# Revit family: Plumbing-Faucet-Sloan-Valve-EFX-380
name_source: partatom
category: Plumbing Fixtures
units: mm (PartAtom-declared; Revit-internal decimal feet)

## family parameters
Cut with Voids When Loaded = No
Host = Face
OmniClass Number = 23.45.55.14
OmniClass Title = Single Faucets
Part Type = Normal
Room Calculation Point = No
Round Connector Dimension = Use Diameter
Shared = No

## types (6) — shared parameters
Assembly Code = D2010
CW Connection = Yes
CWFU = 1.5
Cold Water Connection Diameter = 0"
Default Elevation = 0"
Depth = 6"
Edition number = 1
HW Connection = Yes
HWFU = 1.5
Height = 5"
Hot Water Connection Diameter = 0"
Keynote = 15410
Manufacturer = Sloan Valve
Product Material = Sloan Valve - Finish - Polished Chrome
Product data url = https://bimobject.com
URL = www.sloanvalve.com
Valve Pressure Drop = 0.00 psi
Vent Connection = No
Waste Connection = No
zero-valued in all types: WFU

## per-type parameters (varying)
| type | Description | Part Number | Water Flow | z_Offset | z_Trim Plate 4 |
| EFX-380-4-TUR-BDT-CP-0.5GPM-MLM-CAP-BAA-FCT | 4" Trim Plate, Turbine Power Supply, Below Deck Thermostatic Mixing Valve, Polished Chrome Finish, 0.5 gpm, Multi-Laminar Spray, Capacitance Sensor, BASYS® Turbine-Powered Deck-Mounted Low Body Faucet. | 3324062 | 1 GPM | 3/8" | Yes |
| EFX-380-4-TUR-TEE-CP-0.5GPM-MLM-CAP-BAA-FCT | 4" Trim Plate, Turbine Power Supply, Back-Check Tee, Polished Chrome Finish, 0.5 gpm, Multi-Laminar Spray, Capacitance Sensor, BASYS® Turbine-Powered Deck-Mounted Low Body Faucet. | 3324094 | 1 GPM | 3/8" | Yes |
| EFX-380-TUR-BDT-CP-0.5GPM-MLM-CAP-BAA-FCT | Turbine Power Supply, Below Deck Thermostatic Mixing Valve, Polished Chrome Finish, 0.5 gpm, Multi-Laminar Spray, Capacitance Sensor, BASYS® Turbine-Powered Deck-Mounted Low Body Faucet | 3324235 | 1 GPM | 0" | No |
| EFX-380-TUR-BDT-CP-1.5GPM-CAP-BAA-FCT | Turbine Power Supply, Below Deck Thermostatic Mixing Valve, Polished Chrome Finish, 1.5 gpm, Aerated (installed) or Laminar (in box) Spray, Capacitance Sensor, BASYS® Turbine-Powered Deck Mounted Low Body Faucet. | 3324262 | 2 GPM | 0" | No |
| EFX-380-TUR-TEE-CP-0.5GPM-MLM-CAP-BAA-FCT | Turbine Power Supply, Back-Check Tee, Polished Chrome Finish, 0.5 gpm, Multi-Laminar Spray, Capacitance Sensor, BASYS® Turbine Powered Deck-Mounted Low Body Faucet. | 3324021 | 1 GPM | 0" | No |
| EFX-380-TUR-TEE-CP-1.5GPM-CAP-BAA-FCT | Turbine Power Supply, Back-Check Tee, Polished Chrome Finish, 1.5 gpm, Aerated (installed) or Laminar (in box) Spray, Capacitance Sensor, BASYS® Turbine-Powered Deck-Mounted Low Body Faucet | 3324022 | 2 GPM | 0" | No |

note: column(s) folded — value = type name in every type: Model

## geometry (parser evidence)
native form markers: Sweep x7
no freeform markers — native parametric forms only
